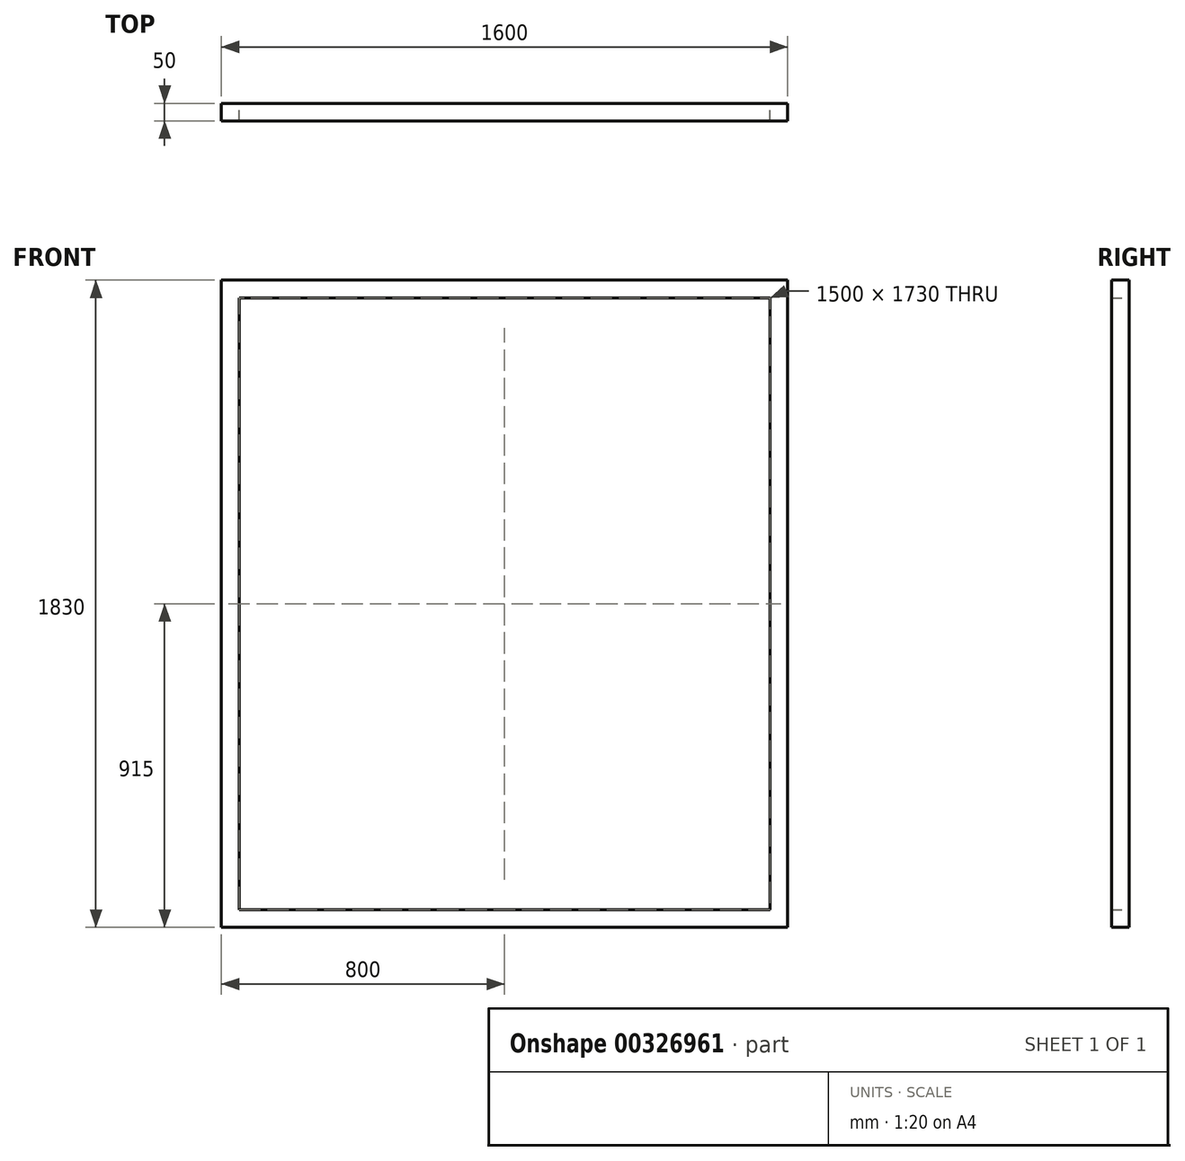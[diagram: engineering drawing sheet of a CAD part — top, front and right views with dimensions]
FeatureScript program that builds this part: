
annotation { "Feature Type Name" : "Feature", "Feature Type Description" : "" }
export const myFeature = defineFeature(function(context is Context, id is Id, definition is map)
    precondition{}
    {
        {
            var Q0;
            Q0=qCreatedBy(makeId("Front.planeOp"),FACE);
            var sketch = newSketch(context, id + "F0", { "sketchPlane" : qUnion([Q0])});
            skLineSegment(sketch, "E0", {"start": v(0, 0) * mm, "end": v(1600, 0) * mm});
            skLineSegment(sketch, "E1", {"start": v(1600, 0) * mm, "end": v(1600, -1830) * mm});
            skLineSegment(sketch, "E2", {"start": v(1600, -1830) * mm, "end": v(0, -1830) * mm});
            skLineSegment(sketch, "E3", {"start": v(0, -1830) * mm, "end": v(0, 0) * mm});
            skLineSegment(sketch, "E4", {"start": v(1600, 0) * mm, "end": v(1550, 0) * mm});
            skLineSegment(sketch, "E5", {"start": v(1550, 0) * mm, "end": v(1550, -50) * mm});
            skLineSegment(sketch, "E6", {"start": v(1550, -50) * mm, "end": v(50, -50) * mm});
            skLineSegment(sketch, "E7", {"start": v(50, -50) * mm, "end": v(50, -1780) * mm});
            skLineSegment(sketch, "E8", {"start": v(50, -1780) * mm, "end": v(1550, -1780) * mm});
            skLineSegment(sketch, "E9", {"start": v(1550, -1780) * mm, "end": v(1550, -50) * mm});
            skSolve(sketch);
        }
        {
            var Q0;
            Q0 = qSketchRegion(id + "F0", true);
            extrude(context, id + "F1", {"entities" : qUnion([Q0]), "depth" : 50 * mm});
        }
    });
